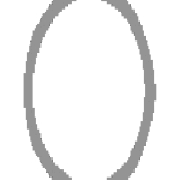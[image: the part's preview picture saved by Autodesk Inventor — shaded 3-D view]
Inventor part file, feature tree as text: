
AUTODESK INVENTOR PART (.ipt)
format: ipt  version: 2021 (Build 250183000, 183)  size: 110,080 bytes
history: native  units: in
note: dims shown in document units (in); Inventor stores cm internally (conversion verified against a paired STEP export)
features: other x4, sketch x3, plane x1
ambient origin geometry x8: Origin, YZ Plane, XZ Plane, XY Plane, X Axis, Y Axis, Z Axis, Center Point
bodies: Solid1 (feature_tree), Body (feature_tree)
feature tree (8):
  other  "Driven Length"
  other  "Frame Generator"
  other  "Start Plane"
  other  "End Plane"
  sketch  "Sketch"  dims[d2=16.9706in d4=-0.0in d5=16.9706in d6=0.12in d7=0.0in d8=90.0deg d9=16.9706in]
  sketch  "Sketch2"  dims[d0=1.0in]
  plane  "Work Plane3"
  sketch  "Sketch3"  dims[d1=0.065in]
